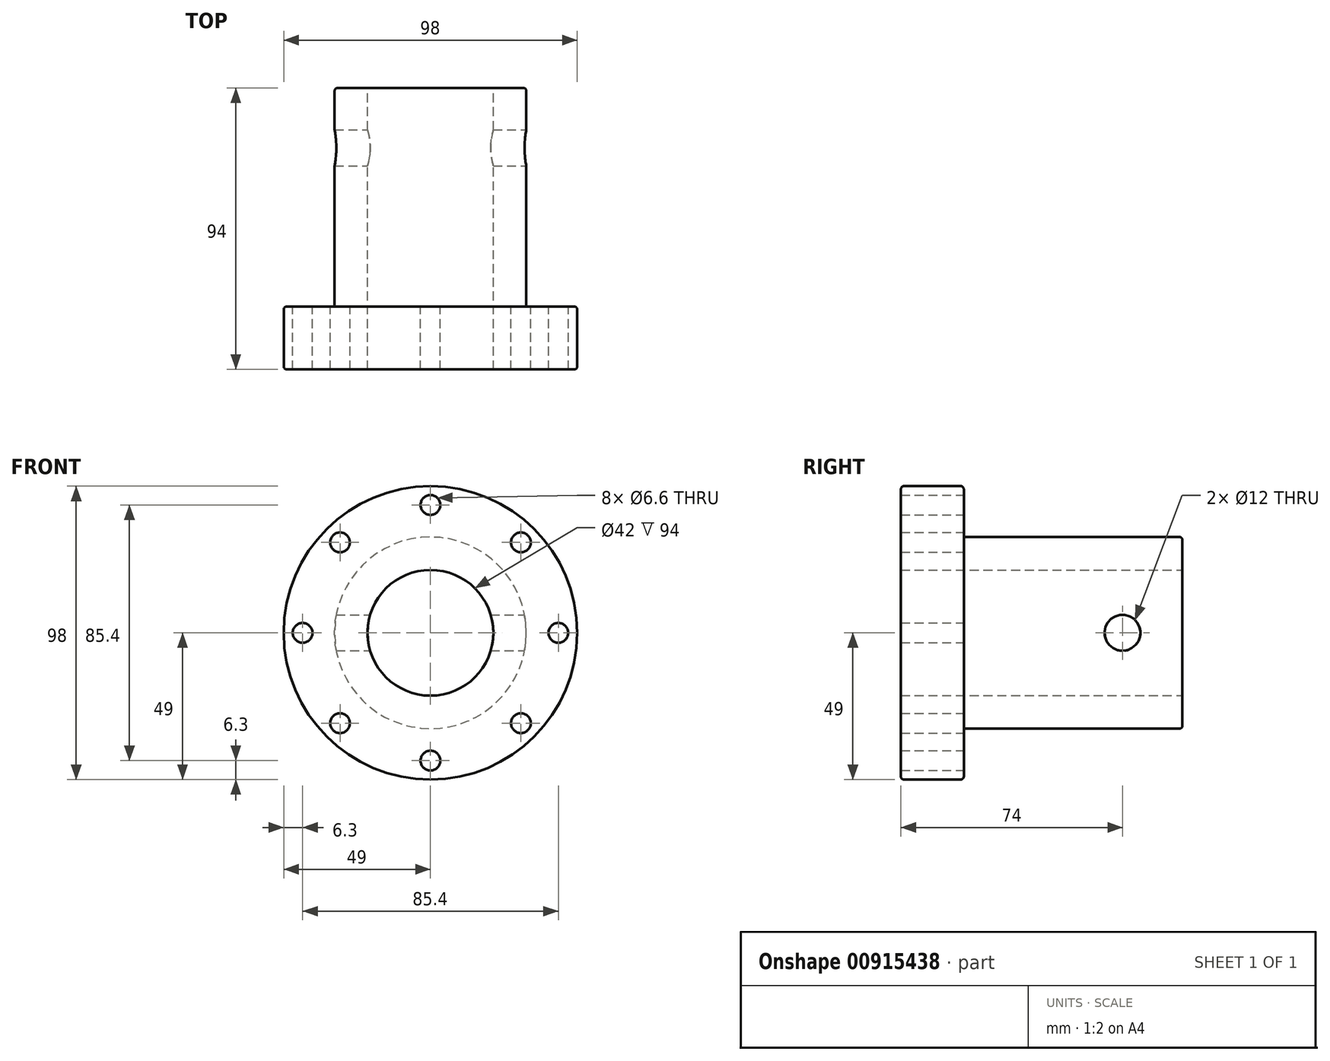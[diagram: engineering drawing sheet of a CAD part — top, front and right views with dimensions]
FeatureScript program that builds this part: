
annotation { "Feature Type Name" : "Feature", "Feature Type Description" : "" }
export const myFeature = defineFeature(function(context is Context, id is Id, definition is map)
    precondition{}
    {
        {
            var Q0;
            Q0=qCreatedBy(makeId("Front.planeOp"),FACE);
            var sketch = newSketch(context, id + "F0", { "sketchPlane" : qUnion([Q0])});
            skCircle(sketch, "E0", {"center": v(0, 0) * mm, "radius": 49 * mm});
            skSolve(sketch);
        }
        {
            var Q0;
            Q0 = qSketchRegion(id + "F0", true);
            extrude(context, id + "F1", {"entities" : qUnion([Q0]), "oppositeDirection" : true, "depth" : 21 * mm, "offsetDistance" : 25 * mm});
        }
        {
            var Q0;
            Q0=makeQuery(id+"F1.opExtrude","CAP_FACE",FACE,{"disambiguationData":[OSD([sQuery(id+"F0.wireOp",EDGE,"E0")])],"isStart":false});
            var sketch = newSketch(context, id + "F2", { "sketchPlane" : qUnion([Q0])});
            skCircle(sketch, "E1", {"center": v(0, 0) * mm, "radius": 32 * mm});
            skSolve(sketch);
        }
        {
            var Q0;
            Q0=makeQuery(id+"F2.imprint","IMPRINT",FACE,{"disambiguationData":[TD([[makeQuery(id+"F2.imprint","IMPRINT",EDGE,{"derivedFrom":sQuery(id+"F2.wireOp",EDGE,"E1")}),1.0]])]});
            extrude(context, id + "F3", {"entities" : qUnion([Q0]), "operationType" : NewBodyOperationType.ADD, "depth" : 73 * mm, "offsetDistance" : 25 * mm});
        }
        {
            var Q0;
            Q0=makeQuery(id+"F3.opExtrude","CAP_FACE",FACE,{"disambiguationData":[OSD([sQuery(id+"F2.wireOp",EDGE,"E1")])],"isStart":false});
            var sketch = newSketch(context, id + "F4", { "sketchPlane" : qUnion([Q0])});
            skCircle(sketch, "E2", {"center": v(0, 0) * mm, "radius": 21 * mm});
            skSolve(sketch);
        }
        {
            var Q0;
            Q0 = qSketchRegion(id + "F4", true);
            extrude(context, id + "F5", {"entities" : qUnion([Q0]), "operationType" : NewBodyOperationType.REMOVE, "oppositeDirection" : true, "depth" : 95 * mm, "offsetDistance" : 25 * mm});
        }
        {
            var Q0;
            Q0=makeQuery(id+"F1.opExtrude","CAP_FACE",FACE,{"disambiguationData":[OSD([sQuery(id+"F0.wireOp",EDGE,"E0")])],"isStart":false});
            var sketch = newSketch(context, id + "F6", { "sketchPlane" : qUnion([Q0])});
            skCircle(sketch, "E3", {"center": v(-30.2, 30.2) * mm, "radius": 3.3 * mm});
            skCircle(sketch, "E4", {"center": v(0, 42.7) * mm, "radius": 3.3 * mm});
            skCircle(sketch, "E5", {"center": v(30.2, 30.2) * mm, "radius": 3.3 * mm});
            skCircle(sketch, "E6.MirrorC", {"center": v(-30.2, -30.2) * mm, "radius": 3.3 * mm});
            skCircle(sketch, "E7.MirrorC", {"center": v(0, -42.7) * mm, "radius": 3.3 * mm});
            skCircle(sketch, "E8.MirrorC", {"center": v(30.2, -30.2) * mm, "radius": 3.3 * mm});
            skCircle(sketch, "E9", {"center": v(-42.7, 0) * mm, "radius": 3.3 * mm});
            skCircle(sketch, "E10", {"center": v(42.7, 0) * mm, "radius": 3.3 * mm});
            skSolve(sketch);
        }
        {
            var Q0;
            Q0 = qSketchRegion(id + "F6", true);
            extrude(context, id + "F7", {"entities" : qUnion([Q0]), "operationType" : NewBodyOperationType.REMOVE, "oppositeDirection" : true, "depth" : 22 * mm, "offsetDistance" : 25 * mm});
        }
        {
            var Q0;
            Q0=qCreatedBy(makeId("Right.planeOp"),FACE);
            var sketch = newSketch(context, id + "F8", { "sketchPlane" : qUnion([Q0])});
            skCircle(sketch, "E11", {"center": v(74, 0) * mm, "radius": 6 * mm});
            skSolve(sketch);
        }
        {
            var Q0;
            Q0 = qSketchRegion(id + "F8", true);
            extrude(context, id + "F9", {"entities" : qUnion([Q0]), "operationType" : NewBodyOperationType.REMOVE, "endBound" : BoundingType.SYMMETRIC, "oppositeDirection" : true, "depth" : 65 * mm, "offsetDistance" : 25 * mm});
        }
        {
            var Q0;
            Q0=makeQuery(id+"F1.opExtrude","CAP_EDGE",EDGE,{"disambiguationData":[OSD([sQuery(id+"F0.wireOp",EDGE,"E0")])],"isStart":true});
            var Q1;
            Q1=makeQuery(id+"F1.opExtrude","CAP_EDGE",EDGE,{"disambiguationData":[OSD([sQuery(id+"F0.wireOp",EDGE,"E0")])],"isStart":false});
            var Q2;
            Q2=makeQuery(id+"F3.opExtrude","CAP_EDGE",EDGE,{"disambiguationData":[OSD([sQuery(id+"F2.wireOp",EDGE,"E1")])],"isStart":false});
            var Q3;
            Q3=makeQuery(id+"F5.boolean.opBoolean","COPY",EDGE,{"derivedFrom":makeQuery(id+"F5.opExtrude","CAP_EDGE",EDGE,{"disambiguationData":[OSD([sQuery(id+"F4.wireOp",EDGE,"E2")])],"isStart":true})});
            var Q4;
            Q4=makeQuery(id+"F3.opExtrude","CAP_EDGE",EDGE,{"disambiguationData":[OSD([sQuery(id+"F2.wireOp",EDGE,"E1")])],"isStart":true});
            fillet(context, id + "F10", {"entities" : qUnion([Q0, Q1, Q2, Q3, Q4]), "radius" : 1 * mm, "tangentPropagation" : true, "defaultsChanged" : false, "vertexSettings" : [], "allowEdgeOverflow" : false});
        }
    });
